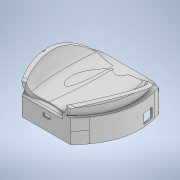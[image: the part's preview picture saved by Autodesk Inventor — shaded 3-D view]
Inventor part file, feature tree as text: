
AUTODESK INVENTOR PART (.ipt)
format: ipt  version: 2022 (Build 260153000, 153)  size: 2,283,520 bytes
history: native  units: mm
features: extrude x44, sketch x22, other x16, fillet x6, loft x1, shell x1, projected_geometry x1
ambient origin geometry x8: Origin, YZ Plane, XZ Plane, XY Plane, X Axis, Y Axis, Z Axis, Center Point
bodies: Body1 (feature_tree)
feature tree (91):
  other  "솔리드2"
  sketch  "스케치3"
  other  "작업 평면1"
  other  "작업 평면3"
  other  "작업 평면4"
  sketch  "스케치9"
  sketch  "스케치10"
  sketch  "스케치11"
  loft  "로프트1"
  shell  "쉘1"  Thickness=20.0mm
  fillet  "모깎기2"  [1 undecoded]
  extrude  "돌출3"  Depth=40.0mm
  extrude  "돌출5"  Depth=55.0mm
  extrude  "돌출6"  Depth=40.0mm
  sketch  "스케치21"
  sketch  "스케치22"
  sketch  "스케치23"
  sketch  "스케치24"
  extrude  "돌출9"  Depth=45.0mm
  extrude  "돌출10"  Depth=25.0mm
  extrude  "돌출11"  TaperAngle=0.0deg  [1 undecoded]
  fillet  "모깎기3"  [1 undecoded]
  other  "작업 평면9"
  sketch  "스케치28"
  other  "작업 평면11"
  extrude  "돌출12"  TaperAngle=0.0deg  [1 undecoded]
  fillet  "모깎기4"  Radius=5.0mm
  other  "작업 평면13"
  other  "작업 평면14"
  extrude  "돌출14"  Depth=110.605575mm
  extrude  "돌출15"  Depth=20.0mm
  sketch  "스케치32"
  extrude  "돌출16"  Depth=20.0mm
  extrude  "돌출17"  Depth=20.0mm
  fillet  "모깎기5"  Radius=20.0mm
  other  "작업 평면15"
  sketch  "스케치34"
  extrude  "돌출18"  Depth=20.0mm
  extrude  "돌출19"  Depth=1.677mm
  extrude  "돌출20"  Depth=1.677mm
  extrude  "돌출21"  Depth=1.677mm
  extrude  "돌출22"  Depth=1.677mm
  extrude  "돌출23"  Depth=88.385mm
  extrude  "돌출24"  Depth=44.1925mm
  extrude  "돌출25"  Depth=10.0mm
  extrude  "돌출26"  Depth=12.5mm
  extrude  "돌출27"  Depth=5.0mm TaperAngle=0.0deg
  extrude  "돌출28"  Depth=5.0mm TaperAngle=0.0deg
  sketch  "스케치35"
  sketch  "스케치36"
  extrude  "돌출29"  Depth=5.0mm TaperAngle=0.0deg
  extrude  "돌출30"  Depth=2.0mm
  other  "작업 평면16"
  sketch  "스케치37"
  extrude  "돌출31"  Depth=3.0mm TaperAngle=0.0deg
  extrude  "돌출32"  Depth=3.0mm TaperAngle=0.0deg
  extrude  "돌출33"  Depth=3.0mm TaperAngle=0.0deg
  extrude  "돌출34"  Depth=9.0mm
  extrude  "돌출35"  TaperAngle=0.0deg  [1 undecoded]
  extrude  "돌출36"  [1 undecoded]
  extrude  "돌출37"  Depth=50.0mm TaperAngle=0.0deg
  extrude  "돌출38"  Depth=2.0mm
  sketch  "스케치40"
  extrude  "돌출40"  Depth=30.0mm TaperAngle=30.0deg
  extrude  "돌출41"  Depth=6.108652mm
  extrude  "돌출42"  Depth=20.0mm
  other  "작업 평면17"
  sketch  "스케치42"
  extrude  "돌출43"  Depth=20.0mm
  extrude  "돌출44"  Depth=30.0mm TaperAngle=0.0deg
  extrude  "돌출45"  Depth=1.677mm
  extrude  "돌출46"  Depth=1.677mm
  other  "작업 평면18"
  extrude  "돌출47"  Depth=20.0mm TaperAngle=0.0deg
  extrude  "돌출48"  Depth=20.0mm
  extrude  "돌출49"  Depth=10.0mm
  extrude  "돌출50"  Depth=2.0mm
  fillet  "모깎기6"  Radius=2.0mm
  other  "작업 평면19"
  sketch  "스케치45"
  fillet  "모깎기7"  Radius=3.0mm
  extrude  "돌출57"  Depth=3.0mm TaperAngle=0.0deg
  other  "작업 평면2"
  other  "작업 평면10"
  sketch  "스케치29"
  other  "작업 평면12"
  sketch  "스케치33"
  sketch  "스케치41"
  sketch  "스케치43"
  sketch  "스케치44"
  projected_geometry  "투영된 루프2"
note: 6 required parameter values undecoded (feature->parameter linkage not recoverable at this tier; creation-order binding heuristic only, values carry confidence <= 0.55)
